# Revit family: Injektionssystem VMU plus, gvz
name_source: partatom
category: HLS-Bauteile
revit_build: Autodesk Revit 2017 (Build: 20190507_1515(x64)
units: mm (PartAtom-declared; Revit-internal decimal feet)

## family parameters
Basisbauteil = Fläche
Beim Laden mit Abzugskörper schneiden = Nein
Bemaßung runder Anschluss = Durchmesser verwenden
Gemeinsam genutzt = Ja
Raumberechnungspunkt = Nein
Teiletyp = Normal

## types (13) — shared parameters
Anwendungsbereich = Beton und Mauerwerk
Brandschutz = ja
Fabrikat = MKT
Festigkeitsklasse = 5.8
Firma = MEFA Befestigungs- und Montagesysteme GmbH
Material = Stahl
Mengeneinheit = St
Oberflaeche = galvanisch verzinkt
Vorgabe-Ansicht = 1219 mm
vpe = 10 St

## per-type parameters (varying)
- Ankerstange VMU-A M 8x110, gvz: Artikelnummer=221831515101; Bohrerdurchmesser (Beton)=10 mm; Bohrerdurchmesser (Vollstein)=10 mm; Bohrlochtiefe (Beton)=80 mm; Bohrlochtiefe (Vollstein)=80 mm; D=7 mm  [stored 0.0229659 ft]; EAN=4043315065100; Gewicht=0.05 kg; Gewicht pro Bauteil=0.05 kg; Gewinde=M8; Kurztext1=Ankerstange VMU plus A M8; Kurztext2=Länge 110 mm; L=110 mm  [stored 0.360892 ft]; L1=95 mm; L2=15 mm  [stored 0.0492126 ft]; Länge=110 mm  [stored 0.360892 ft]; Länge Dübel=110 mm  [stored 0.360892 ft]; Mutter=Sechskantmutter : Sechskantmutter M8; Schlüsselweite=13; Unterlegscheibe=Unterlegscheibe : Unterlegscheibe 8.4x16x1.6; max. Klemmstärke (Beton)=20 mm; max. Klemmstärke (Vollstein)=20 mm; max. Klemmstärke bei Siebhülse 16x85=15 mm
- Ankerstange VMU-A M10x110, gvz: Artikelnummer=221831605101; Bohrerdurchmesser (Beton)=12 mm; Bohrerdurchmesser (Vollstein)=12 mm; Bohrlochtiefe (Beton)=90 mm; Bohrlochtiefe (Vollstein)=90 mm; D=8 mm  [stored 0.0262467 ft]; EAN=4250928457684; Gewicht=0.08 kg; Gewicht pro Bauteil=0.08 kg; Gewinde=M10; Kurztext1=Ankerstange VMU plus A M10; Kurztext2=Länge 110 mm; L=110 mm  [stored 0.360892 ft]; L1=95 mm; L2=15 mm  [stored 0.0492126 ft]; Länge=110 mm  [stored 0.360892 ft]; Länge Dübel=110 mm  [stored 0.360892 ft]; Mutter=Sechskantmutter : Sechskantmutter M10; Schlüsselweite=17; Unterlegscheibe=Unterlegscheibe : Unterlegscheibe 10.5x20x2; max. Klemmstärke (Beton)=10 mm; max. Klemmstärke (Vollstein)=10 mm; max. Klemmstärke bei Siebhülse 16x85=15 mm
- Ankerstange VMU-A M12x135, gvz: Artikelnummer=221831710101; Bohrerdurchmesser (Beton)=14 mm; Bohrerdurchmesser (Vollstein)=14 mm; Bohrlochtiefe (Beton)=110 mm; Bohrlochtiefe (Vollstein)=90 mm; D=10 mm  [stored 0.0328084 ft]; EAN=4250928457707; Gewicht=0.13 kg; Gewicht pro Bauteil=0.13 kg; Gewinde=M12; Kurztext1=Ankerstange VMU plus A M12; Kurztext2=Länge 135 mm; L=135 mm  [stored 0.442913 ft]; L1=120 mm  [stored 0.393701 ft]; L2=15 mm  [stored 0.0492126 ft]; Länge=135 mm  [stored 0.442913 ft]; Länge Dübel=135 mm  [stored 0.442913 ft]; Mutter=Sechskantmutter : Sechskantmutter M12; Schlüsselweite=19; Unterlegscheibe=Unterlegscheibe : Unterlegscheibe 13x24x2.5; max. Klemmstärke (Beton)=10 mm; max. Klemmstärke (Vollstein)=20 mm; max. Klemmstärke bei Siebhülse 20x85=35 mm
- Ankerstange VMU-A M16x160, gvz: Artikelnummer=221831810101; Bohrerdurchmesser (Beton)=18 mm; Bohrerdurchmesser (Vollstein)=18 mm; Bohrlochtiefe (Beton)=110 mm; Bohrlochtiefe (Vollstein)=100 mm; D=14 mm  [stored 0.0459318 ft]; EAN=4250928457721; Gewicht=0.27 kg; Gewicht pro Bauteil=0.27 kg; Gewinde=M16; Kurztext1=Ankerstange VMU plus A M16; Kurztext2=Länge 160 mm; L=160 mm  [stored 0.524934 ft]; L1=140 mm  [stored 0.459318 ft]; L2=20 mm  [stored 0.0656168 ft]; Länge=160 mm  [stored 0.524934 ft]; Länge Dübel=160 mm  [stored 0.524934 ft]; Mutter=Sechskantmutter : Sechskantmutter M16; Schlüsselweite=24; Unterlegscheibe=Unterlegscheibe : Unterlegscheibe, verstärkt 17x44x3.5; max. Klemmstärke (Beton)=15 mm; max. Klemmstärke (Vollstein)=40 mm; max. Klemmstärke bei Siebhülse 20x130=10 mm; max. Klemmstärke bei Siebhülse 20x85=55 mm
- Ankerstange VMU-A M 8x130, gvz: Artikelnummer=221831525101; Bohrerdurchmesser (Beton)=10 mm; Bohrerdurchmesser (Vollstein)=10 mm; Bohrlochtiefe (Beton)=80 mm; Bohrlochtiefe (Vollstein)=80 mm; D=7 mm  [stored 0.0229659 ft]; EAN=4043315065131; Gewicht=0.05 kg; Gewicht pro Bauteil=0.05 kg; Gewinde=M8; Kurztext1=Ankerstange VMU plus A M8; Kurztext2=Länge 130 mm; L=130 mm  [stored 0.426509 ft]; L1=115 mm  [stored 0.377297 ft]; L2=15 mm  [stored 0.0492126 ft]; Länge=130 mm  [stored 0.426509 ft]; Länge Dübel=130 mm  [stored 0.426509 ft]; Mutter=Sechskantmutter : Sechskantmutter M8; Schlüsselweite=13; Unterlegscheibe=Unterlegscheibe : Unterlegscheibe 8.4x16x1.6; max. Klemmstärke (Beton)=40 mm; max. Klemmstärke (Vollstein)=40 mm; max. Klemmstärke bei Siebhülse 16x85=35 mm
- Ankerstange VMU-A M10x130, gvz: Artikelnummer=221831625101; Bohrerdurchmesser (Beton)=12 mm; Bohrerdurchmesser (Vollstein)=12 mm; Bohrlochtiefe (Beton)=90 mm; Bohrlochtiefe (Vollstein)=90 mm; D=8 mm  [stored 0.0262467 ft]; EAN=4043315064455; Gewicht=0.09 kg; Gewicht pro Bauteil=0.09 kg; Gewinde=M10; Kurztext1=Ankerstange VMU plus A M10; Kurztext2=Länge 130 mm; L=130 mm  [stored 0.426509 ft]; L1=115 mm  [stored 0.377297 ft]; L2=15 mm  [stored 0.0492126 ft]; Länge=130 mm  [stored 0.426509 ft]; Länge Dübel=130 mm  [stored 0.426509 ft]; Mutter=Sechskantmutter : Sechskantmutter M10; Schlüsselweite=17; Unterlegscheibe=Unterlegscheibe : Unterlegscheibe 10.5x20x2; max. Klemmstärke (Beton)=30 mm; max. Klemmstärke (Vollstein)=30 mm; max. Klemmstärke bei Siebhülse 16x85=35 mm
- Ankerstange VMU-A M10x150, gvz: Artikelnummer=221831630101; Bohrerdurchmesser (Beton)=12 mm; Bohrerdurchmesser (Vollstein)=12 mm; Bohrlochtiefe (Beton)=90 mm; Bohrlochtiefe (Vollstein)=90 mm; D=8 mm  [stored 0.0262467 ft]; EAN=4043315064486; Gewicht=0.10 kg; Gewicht pro Bauteil=0.10 kg; Gewinde=M10; Kurztext1=Ankerstange VMU plus A M10; Kurztext2=Länge 150 mm; L=150 mm; L1=135 mm  [stored 0.442913 ft]; L2=15 mm  [stored 0.0492126 ft]; Länge=150 mm; Länge Dübel=150 mm; Mutter=Sechskantmutter : Sechskantmutter M10; Schlüsselweite=17; Unterlegscheibe=Unterlegscheibe : Unterlegscheibe 10.5x20x2; max. Klemmstärke (Beton)=50 mm; max. Klemmstärke (Vollstein)=50 mm; max. Klemmstärke bei Siebhülse 16x130=10 mm; max. Klemmstärke bei Siebhülse 16x85=55 mm
- Ankerstange VMU-A M10x165, gvz: Artikelnummer=221831635101; Bohrerdurchmesser (Beton)=12 mm; Bohrerdurchmesser (Vollstein)=12 mm; Bohrlochtiefe (Beton)=90 mm; Bohrlochtiefe (Vollstein)=90 mm; D=8 mm  [stored 0.0262467 ft]; EAN=4043315064516; Gewicht=0.10 kg; Gewicht pro Bauteil=0.10 kg; Gewinde=M10; Kurztext1=Ankerstange VMU plus A M10; Kurztext2=Länge 165 mm; L=165 mm  [stored 0.541339 ft]; L1=150 mm; L2=15 mm  [stored 0.0492126 ft]; Länge=165 mm  [stored 0.541339 ft]; Länge Dübel=165 mm  [stored 0.541339 ft]; Mutter=Sechskantmutter : Sechskantmutter M10; Schlüsselweite=17; Unterlegscheibe=Unterlegscheibe : Unterlegscheibe 10.5x20x2; max. Klemmstärke (Beton)=65 mm; max. Klemmstärke (Vollstein)=65 mm; max. Klemmstärke bei Siebhülse 16x130=25 mm; max. Klemmstärke bei Siebhülse 16x85=70 mm
- Ankerstange VMU-A M10x190, gvz: Artikelnummer=221831645101; Bohrerdurchmesser (Beton)=12 mm; Bohrerdurchmesser (Vollstein)=12 mm; Bohrlochtiefe (Beton)=90 mm; Bohrlochtiefe (Vollstein)=90 mm; D=8 mm  [stored 0.0262467 ft]; EAN=4250928457691; Gewicht=0.12 kg; Gewicht pro Bauteil=0.12 kg; Gewinde=M10; Kurztext1=Ankerstange VMU plus A M10; Kurztext2=Länge 190 mm; L=190 mm; L1=175 mm  [stored 0.574147 ft]; L2=15 mm  [stored 0.0492126 ft]; Länge=190 mm; Länge Dübel=190 mm; Mutter=Sechskantmutter : Sechskantmutter M10; Schlüsselweite=17; Unterlegscheibe=Unterlegscheibe : Unterlegscheibe 10.5x20x2; max. Klemmstärke (Beton)=90 mm; max. Klemmstärke (Vollstein)=90 mm; max. Klemmstärke bei Siebhülse 16x130=50 mm; max. Klemmstärke bei Siebhülse 16x85=95 mm
- Ankerstange VMU-A M12x155, gvz: Artikelnummer=221831720101; Bohrerdurchmesser (Beton)=14 mm; Bohrerdurchmesser (Vollstein)=14 mm; Bohrlochtiefe (Beton)=110 mm; Bohrlochtiefe (Vollstein)=90 mm; D=10 mm  [stored 0.0328084 ft]; EAN=4043315065223; Gewicht=0.14 kg; Gewicht pro Bauteil=0.14 kg; Gewinde=M12; Kurztext1=Ankerstange VMU plus A M12; Kurztext2=Länge 155 mm; L=155 mm  [stored 0.50853 ft]; L1=140 mm  [stored 0.459318 ft]; L2=15 mm  [stored 0.0492126 ft]; Länge=155 mm  [stored 0.50853 ft]; Länge Dübel=155 mm  [stored 0.50853 ft]; Mutter=Sechskantmutter : Sechskantmutter M12; Schlüsselweite=19; Unterlegscheibe=Unterlegscheibe : Unterlegscheibe 13x24x2.5; max. Klemmstärke (Beton)=30 mm; max. Klemmstärke (Vollstein)=40 mm; max. Klemmstärke bei Siebhülse 20x130=10 mm; max. Klemmstärke bei Siebhülse 20x85=55 mm
- Ankerstange VMU-A M12x175, gvz: Artikelnummer=221831730101; Bohrerdurchmesser (Beton)=14 mm; Bohrerdurchmesser (Vollstein)=14 mm; Bohrlochtiefe (Beton)=110 mm; Bohrlochtiefe (Vollstein)=90 mm; D=10 mm  [stored 0.0328084 ft]; EAN=4250928457714; Gewicht=0.15 kg; Gewicht pro Bauteil=0.15 kg; Gewinde=M12; Kurztext1=Ankerstange VMU plus A M12; Kurztext2=Länge 175 mm; L=175 mm  [stored 0.574147 ft]; L1=160 mm  [stored 0.524934 ft]; L2=15 mm  [stored 0.0492126 ft]; Länge=175 mm  [stored 0.574147 ft]; Länge Dübel=175 mm  [stored 0.574147 ft]; Mutter=Sechskantmutter : Sechskantmutter M12; Schlüsselweite=19; Unterlegscheibe=Unterlegscheibe : Unterlegscheibe 13x24x2.5; max. Klemmstärke (Beton)=50 mm; max. Klemmstärke (Vollstein)=60 mm; max. Klemmstärke bei Siebhülse 20x130=30 mm; max. Klemmstärke bei Siebhülse 20x85=75 mm
- Ankerstange VMU-A M12x210, gvz: Artikelnummer=221831740101; Bohrerdurchmesser (Beton)=14 mm; Bohrerdurchmesser (Vollstein)=14 mm; Bohrlochtiefe (Beton)=110 mm; Bohrlochtiefe (Vollstein)=90 mm; D=10 mm  [stored 0.0328084 ft]; EAN=4043315064707; Gewicht=0.18 kg; Gewicht pro Bauteil=0.18 kg; Gewinde=M12; Kurztext1=Ankerstange VMU plus A M12; Kurztext2=Länge 210 mm; L=210 mm  [stored 0.688976 ft]; L1=195 mm  [stored 0.639764 ft]; L2=15 mm  [stored 0.0492126 ft]; Länge=210 mm  [stored 0.688976 ft]; Länge Dübel=210 mm  [stored 0.688976 ft]; Mutter=Sechskantmutter : Sechskantmutter M12; Schlüsselweite=19; Unterlegscheibe=Unterlegscheibe : Unterlegscheibe 13x24x2.5; max. Klemmstärke (Beton)=85 mm; max. Klemmstärke (Vollstein)=95 mm; max. Klemmstärke bei Siebhülse 20x130=65 mm; max. Klemmstärke bei Siebhülse 20x85=110 mm
- Ankerstange VMU-A M16x175, gvz: Artikelnummer=221831815101; Bohrerdurchmesser (Beton)=18 mm; Bohrerdurchmesser (Vollstein)=18 mm; Bohrlochtiefe (Beton)=110 mm; Bohrlochtiefe (Vollstein)=100 mm; D=14 mm  [stored 0.0459318 ft]; EAN=4250928457738; Gewicht=0.29 kg; Gewicht pro Bauteil=0.29 kg; Gewinde=M16; Kurztext1=Ankerstange VMU plus A M16; Kurztext2=Länge 175 mm; L=175 mm  [stored 0.574147 ft]; L1=155 mm  [stored 0.50853 ft]; L2=20 mm  [stored 0.0656168 ft]; Länge=175 mm  [stored 0.574147 ft]; Länge Dübel=175 mm  [stored 0.574147 ft]; Mutter=Sechskantmutter : Sechskantmutter M16; Schlüsselweite=24; Unterlegscheibe=Unterlegscheibe : Unterlegscheibe, verstärkt 17x44x3.5; max. Klemmstärke (Beton)=30 mm; max. Klemmstärke (Vollstein)=55 mm; max. Klemmstärke bei Siebhülse 20x130=25 mm; max. Klemmstärke bei Siebhülse 20x85=70 mm

note: [stored X ft] marks values corroborated as IEEE doubles in the binary element streams (Revit-internal decimal feet)

## geometry (parser evidence)
native form markers: Sweep x3
no freeform markers — native parametric forms only
